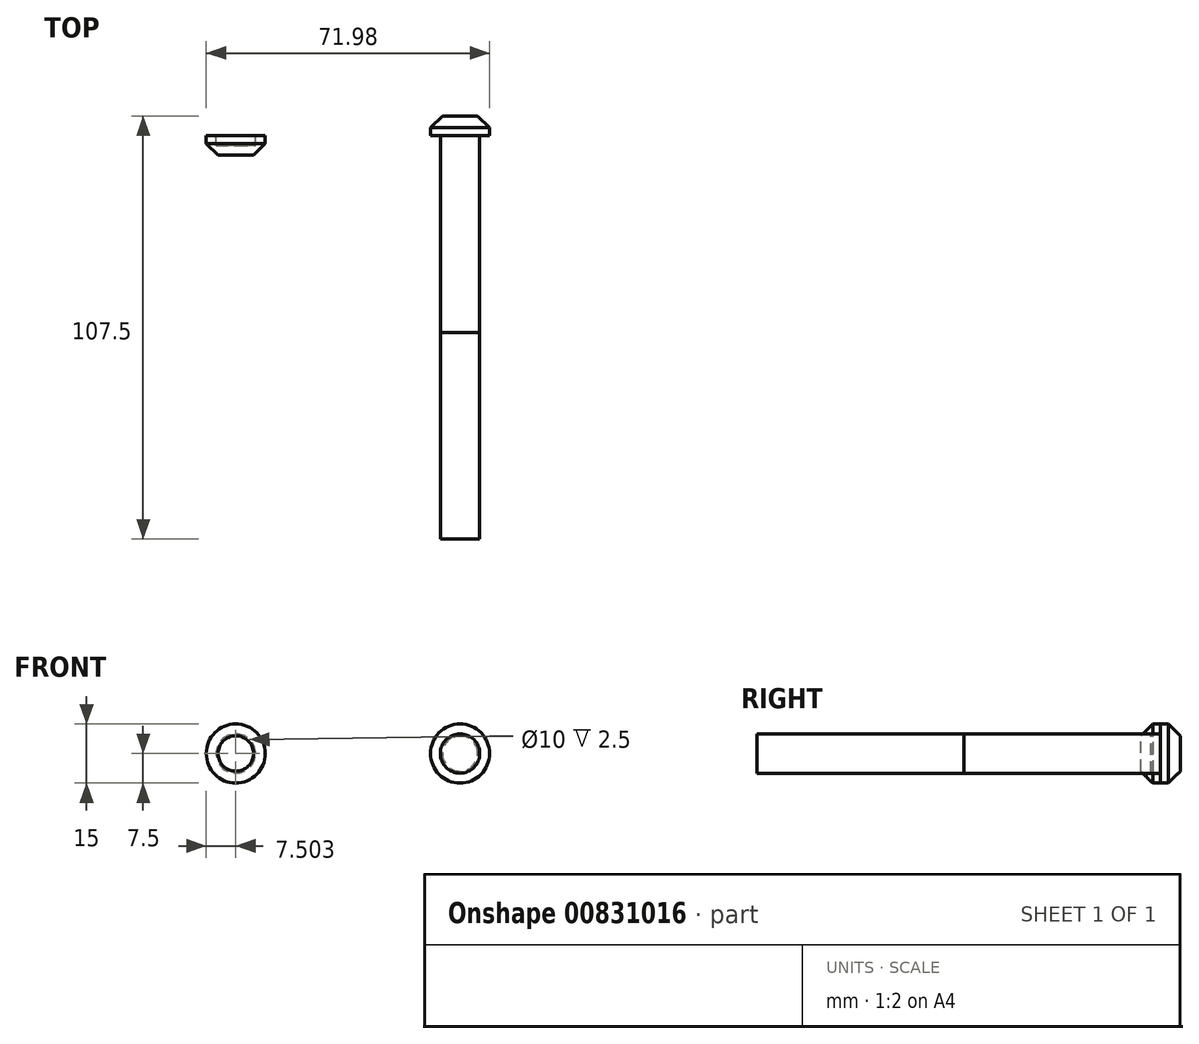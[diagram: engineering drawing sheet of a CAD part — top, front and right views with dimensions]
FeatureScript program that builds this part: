
annotation { "Feature Type Name" : "Feature", "Feature Type Description" : "" }
export const myFeature = defineFeature(function(context is Context, id is Id, definition is map)
    precondition{}
    {
        {
            var Q0;
            Q0=qCreatedBy(makeId("Front.planeOp"),FACE);
            var sketch = newSketch(context, id + "F0", { "sketchPlane" : qUnion([Q0])});
            skCircle(sketch, "E0", {"center": v(0, 0) * mm, "radius": 5 * mm});
            skCircle(sketch, "E1", {"center": v(0, 0) * mm, "radius": 7.5 * mm});
            skCircle(sketch, "E2", {"center": v(-56.98, 0) * mm, "radius": 5 * mm});
            skCircle(sketch, "E3", {"center": v(-56.98, 0) * mm, "radius": 7.5 * mm});
            skSolve(sketch);
        }
        {
            var Q0;
            Q0=makeQuery(id+"F0.imprint","IMPRINT",FACE,{"disambiguationData":[TD([[makeQuery(id+"F0.imprint","IMPRINT",EDGE,{"derivedFrom":sQuery(id+"F0.wireOp",EDGE,"E0")}),1.0]])]});
            var Q1;
            Q1=makeQuery(id+"F0.imprint","IMPRINT",FACE,{"disambiguationData":[TD([[makeQuery(id+"F0.imprint","IMPRINT",EDGE,{"derivedFrom":sQuery(id+"F0.wireOp",EDGE,"E0")}),-1.0]])]});
            extrude(context, id + "F1", {"entities" : qUnion([Q0, Q1]), "oppositeDirection" : true, "depth" : 5 * mm, "offsetDistance" : 25 * mm});
        }
        {
            var Q0;
            Q0=makeQuery(id+"F0.imprint","IMPRINT",FACE,{"disambiguationData":[TD([[makeQuery(id+"F0.imprint","IMPRINT",EDGE,{"derivedFrom":sQuery(id+"F0.wireOp",EDGE,"E0")}),1.0]])]});
            extrude(context, id + "F2", {"entities" : qUnion([Q0]), "operationType" : NewBodyOperationType.ADD, "depth" : 50 * mm, "offsetDistance" : 25 * mm});
        }
        {
            var Q0;
            Q0=makeQuery(id+"F2.opExtrude","CAP_FACE",FACE,{"disambiguationData":[OSD([sQuery(id+"F0.wireOp",EDGE,"E0")])],"isStart":false});
            var sketch = newSketch(context, id + "F3", { "sketchPlane" : qUnion([Q0])});
            skCircle(sketch, "E4", {"center": v(0, 0) * mm, "radius": 5 * mm});
            skSolve(sketch);
        }
        {
            var Q0;
            Q0=makeQuery(id+"F3.imprint","IMPRINT",FACE,{"disambiguationData":[TD([[makeQuery(id+"F3.imprint","IMPRINT",EDGE,{"derivedFrom":sQuery(id+"F3.wireOp",EDGE,"E4")}),1.0]])]});
            extrude(context, id + "F4", {"entities" : qUnion([Q0]), "depth" : 52.5 * mm, "offsetDistance" : 25 * mm});
        }
        {
            var Q0;
            Q0=makeQuery(id+"F0.imprint","IMPRINT",FACE,{"disambiguationData":[TD([[makeQuery(id+"F0.imprint","IMPRINT",EDGE,{"derivedFrom":sQuery(id+"F0.wireOp",EDGE,"E2")}),-1.0]])]});
            var Q1;
            Q1=makeQuery(id+"F0.imprint","IMPRINT",FACE,{"disambiguationData":[TD([[makeQuery(id+"F0.imprint","IMPRINT",EDGE,{"derivedFrom":sQuery(id+"F0.wireOp",EDGE,"E2")}),1.0]])]});
            extrude(context, id + "F5", {"entities" : qUnion([Q0, Q1]), "depth" : 5 * mm, "offsetDistance" : 25 * mm});
        }
        {
            var Q0;
            Q0=makeQuery(id+"F0.imprint","IMPRINT",FACE,{"disambiguationData":[TD([[makeQuery(id+"F0.imprint","IMPRINT",EDGE,{"derivedFrom":sQuery(id+"F0.wireOp",EDGE,"E2")}),1.0]])]});
            extrude(context, id + "F6", {"entities" : qUnion([Q0]), "operationType" : NewBodyOperationType.REMOVE, "depth" : 2.5 * mm, "offsetDistance" : 25 * mm});
        }
        {
            var Q0;
            Q0=makeQuery(id+"F1.opExtrude","CAP_EDGE",EDGE,{"disambiguationData":[OSD([sQuery(id+"F0.wireOp",EDGE,"E1")])],"isStart":false});
            chamfer(context, id + "F7", {"entities" : qUnion([Q0]), "width" : 3 * mm, "tangentPropagation" : true});
        }
        {
            var Q0;
            Q0=makeQuery(id+"F5.opExtrude","CAP_EDGE",EDGE,{"disambiguationData":[OSD([sQuery(id+"F0.wireOp",EDGE,"E3")])],"isStart":false});
            chamfer(context, id + "F8", {"entities" : qUnion([Q0]), "width" : 3 * mm, "tangentPropagation" : true});
        }
    });
